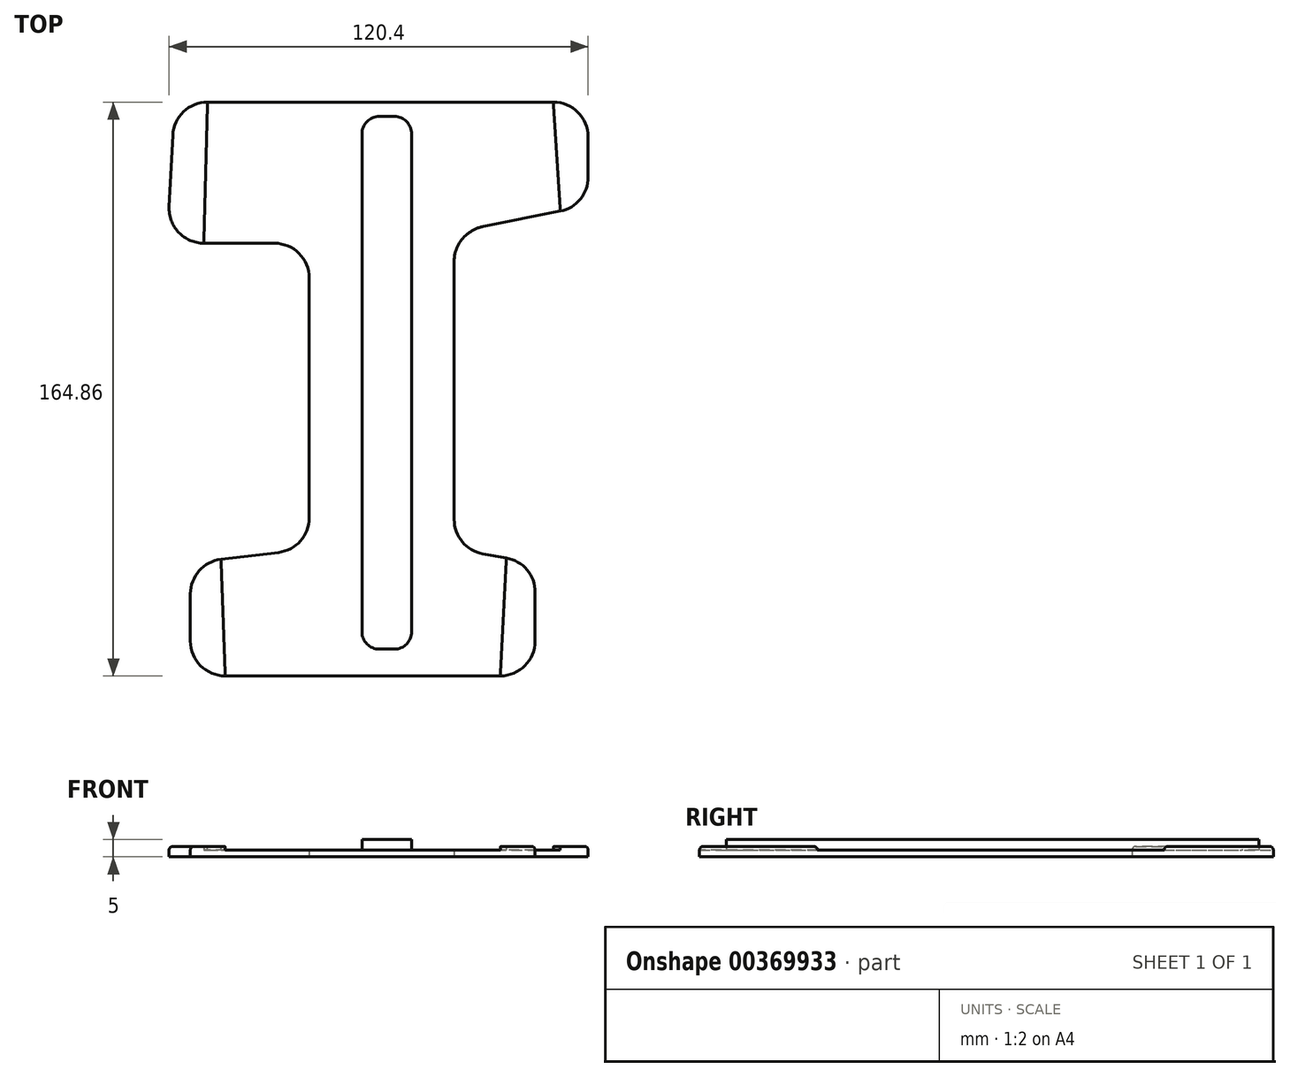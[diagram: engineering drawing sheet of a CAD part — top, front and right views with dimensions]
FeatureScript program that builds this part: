
annotation { "Feature Type Name" : "Feature", "Feature Type Description" : "" }
export const myFeature = defineFeature(function(context is Context, id is Id, definition is map)
    precondition{}
    {
        {
            var Q0;
            Q0=qCreatedBy(makeId("Top.planeOp"),FACE);
            var sketch = newSketch(context, id + "F0", { "sketchPlane" : qUnion([Q0])});
            skLineSegment(sketch, "E0", {"start": v(-44.38, 100.11) * mm, "end": v(55, 100.11) * mm});
            skLineSegment(sketch, "E1", {"start": v(65, 90.11) * mm, "end": v(65, 78.6) * mm});
            skLineSegment(sketch, "E2", {"start": v(56.95, 68.78) * mm, "end": v(34.8, 64.37) * mm});
            skLineSegment(sketch, "E3", {"start": v(30.52, 62.4) * mm, "end": v(30.27, 62.2) * mm});
            skLineSegment(sketch, "E4", {"start": v(26.49, 54.36) * mm, "end": v(26.49, -19.82) * mm});
            skLineSegment(sketch, "E5", {"start": v(34.74, -29.66) * mm, "end": v(41.5, -30.86) * mm});
            skLineSegment(sketch, "E6", {"start": v(49.76, -40.71) * mm, "end": v(49.76, -54.75) * mm});
            skLineSegment(sketch, "E7", {"start": v(39.76, -64.75) * mm, "end": v(-39.3, -64.75) * mm});
            skLineSegment(sketch, "E8", {"start": v(-49.3, -54.75) * mm, "end": v(-49.3, -41.2) * mm});
            skLineSegment(sketch, "E9", {"start": v(-40.5, -31.27) * mm, "end": v(-23.95, -29.26) * mm});
            skLineSegment(sketch, "E10", {"start": v(-15.15, -19.34) * mm, "end": v(-15.15, 49.57) * mm});
            skLineSegment(sketch, "E11", {"start": v(-25.15, 59.57) * mm, "end": v(-45.4, 59.57) * mm});
            skLineSegment(sketch, "E12", {"start": v(-55.4, 70.07) * mm, "end": v(-54.37, 90.6) * mm});
            skPoint(sketch, "E13.visualSharp", {"position": v(-55.91, 59.57) * mm});
            skArc(sketch, "E13.filletArc", {"start": v(-55.4, 70.07) * mm, "mid": v(-52.65, 62.68) * mm, "end": v(-45.4, 59.57) * mm});
            skPoint(sketch, "E14.visualSharp", {"position": v(-15.15, 59.57) * mm});
            skArc(sketch, "E14.filletArc", {"start": v(-15.15, 49.57) * mm, "mid": v(-18.08, 56.64) * mm, "end": v(-25.15, 59.57) * mm});
            skPoint(sketch, "E15.visualSharp", {"position": v(-53.9, 100.11) * mm});
            skArc(sketch, "E15.filletArc", {"start": v(-44.38, 100.11) * mm, "mid": v(-51.28, 97.35) * mm, "end": v(-54.37, 90.6) * mm});
            skPoint(sketch, "E16.visualSharp", {"position": v(65, 100.11) * mm});
            skArc(sketch, "E16.filletArc", {"start": v(65, 90.11) * mm, "mid": v(62.07, 97.18) * mm, "end": v(55, 100.11) * mm});
            skPoint(sketch, "E17.visualSharp", {"position": v(65, 70.39) * mm});
            skArc(sketch, "E17.filletArc", {"start": v(56.95, 68.78) * mm, "mid": v(62.73, 72.25) * mm, "end": v(65, 78.6) * mm});
            skPoint(sketch, "E18.visualSharp", {"position": v(32.42, 63.9) * mm});
            skArc(sketch, "E18.filletArc", {"start": v(34.8, 64.37) * mm, "mid": v(32.54, 63.64) * mm, "end": v(30.52, 62.4) * mm});
            skPoint(sketch, "E19.visualSharp", {"position": v(26.49, 59.2) * mm});
            skArc(sketch, "E19.filletArc", {"start": v(30.27, 62.2) * mm, "mid": v(27.48, 58.71) * mm, "end": v(26.49, 54.36) * mm});
            skPoint(sketch, "E20.visualSharp", {"position": v(-15.15, -28.2) * mm});
            skArc(sketch, "E20.filletArc", {"start": v(-23.95, -29.26) * mm, "mid": v(-17.67, -25.97) * mm, "end": v(-15.15, -19.34) * mm});
            skPoint(sketch, "E21.visualSharp", {"position": v(26.49, -28.2) * mm});
            skArc(sketch, "E21.filletArc", {"start": v(26.49, -19.82) * mm, "mid": v(28.83, -26.24) * mm, "end": v(34.74, -29.66) * mm});
            skPoint(sketch, "E22.visualSharp", {"position": v(49.76, -32.33) * mm});
            skArc(sketch, "E22.filletArc", {"start": v(49.76, -40.71) * mm, "mid": v(47.42, -34.29) * mm, "end": v(41.5, -30.86) * mm});
            skPoint(sketch, "E23.visualSharp", {"position": v(-49.3, -32.33) * mm});
            skArc(sketch, "E23.filletArc", {"start": v(-40.5, -31.27) * mm, "mid": v(-46.78, -34.56) * mm, "end": v(-49.3, -41.2) * mm});
            skPoint(sketch, "E24.visualSharp", {"position": v(49.76, -64.75) * mm});
            skArc(sketch, "E24.filletArc", {"start": v(39.76, -64.75) * mm, "mid": v(46.83, -61.82) * mm, "end": v(49.76, -54.75) * mm});
            skPoint(sketch, "E25.visualSharp", {"position": v(-49.3, -64.75) * mm});
            skArc(sketch, "E25.filletArc", {"start": v(-49.3, -54.75) * mm, "mid": v(-46.37, -61.82) * mm, "end": v(-39.3, -64.75) * mm});
            skSolve(sketch);
        }
        {
            var Q0;
            Q0=makeQuery(id+"F0.imprint","IMPRINT",FACE,{"disambiguationData":[TD([[makeQuery(id+"F0.imprint","IMPRINT",EDGE,{"derivedFrom":sQuery(id+"F0.wireOp",EDGE,"E0")}),-1.0]])]});
            extrude(context, id + "F1", {"entities" : qUnion([Q0]), "depth" : 2 * mm});
        }
        {
            var Q0;
            Q0=makeQuery(id+"F1.opExtrude","CAP_FACE",FACE,{"disambiguationData":[OSD([sQuery(id+"F0.wireOp",EDGE,"E0"),sQuery(id+"F0.wireOp",EDGE,"E1"),sQuery(id+"F0.wireOp",EDGE,"E2"),sQuery(id+"F0.wireOp",EDGE,"E3"),sQuery(id+"F0.wireOp",EDGE,"E4"),sQuery(id+"F0.wireOp",EDGE,"E5"),sQuery(id+"F0.wireOp",EDGE,"E6"),sQuery(id+"F0.wireOp",EDGE,"E7"),sQuery(id+"F0.wireOp",EDGE,"E8"),sQuery(id+"F0.wireOp",EDGE,"E9"),sQuery(id+"F0.wireOp",EDGE,"E10"),sQuery(id+"F0.wireOp",EDGE,"E11"),sQuery(id+"F0.wireOp",EDGE,"E12"),sQuery(id+"F0.wireOp",EDGE,"E13.filletArc"),sQuery(id+"F0.wireOp",EDGE,"E14.filletArc"),sQuery(id+"F0.wireOp",EDGE,"E15.filletArc"),sQuery(id+"F0.wireOp",EDGE,"E16.filletArc"),sQuery(id+"F0.wireOp",EDGE,"E17.filletArc"),sQuery(id+"F0.wireOp",EDGE,"E18.filletArc"),sQuery(id+"F0.wireOp",EDGE,"E19.filletArc"),sQuery(id+"F0.wireOp",EDGE,"E20.filletArc"),sQuery(id+"F0.wireOp",EDGE,"E21.filletArc"),sQuery(id+"F0.wireOp",EDGE,"E22.filletArc"),sQuery(id+"F0.wireOp",EDGE,"E23.filletArc"),sQuery(id+"F0.wireOp",EDGE,"E24.filletArc"),sQuery(id+"F0.wireOp",EDGE,"E25.filletArc")])],"isStart":false});
            var sketch = newSketch(context, id + "F2", { "sketchPlane" : qUnion([Q0])});
            skLineSegment(sketch, "E26", {"start": v(0, 91) * mm, "end": v(0, -52.06) * mm});
            skLineSegment(sketch, "E27", {"start": v(5, -57.06) * mm, "end": v(9.29, -57.06) * mm});
            skLineSegment(sketch, "E28", {"start": v(14.29, -52.06) * mm, "end": v(14.29, 91) * mm});
            skLineSegment(sketch, "E29", {"start": v(9.29, 96) * mm, "end": v(5, 96) * mm});
            skPoint(sketch, "E30.visualSharp", {"position": v(14.29, 96) * mm});
            skArc(sketch, "E30.filletArc", {"start": v(14.29, 91) * mm, "mid": v(12.82, 94.53) * mm, "end": v(9.29, 96) * mm});
            skPoint(sketch, "E31.visualSharp", {"position": v(0, 96) * mm});
            skArc(sketch, "E31.filletArc", {"start": v(5, 96) * mm, "mid": v(1.46, 94.53) * mm, "end": v(0, 91) * mm});
            skPoint(sketch, "E32.visualSharp", {"position": v(14.29, -57.06) * mm});
            skArc(sketch, "E32.filletArc", {"start": v(9.29, -57.06) * mm, "mid": v(12.82, -55.6) * mm, "end": v(14.29, -52.06) * mm});
            skPoint(sketch, "E33.visualSharp", {"position": v(0, -57.06) * mm});
            skArc(sketch, "E33.filletArc", {"start": v(0, -52.06) * mm, "mid": v(1.46, -55.6) * mm, "end": v(5, -57.06) * mm});
            skSolve(sketch);
        }
        {
            var Q0;
            Q0=makeQuery(id+"F2.imprint","IMPRINT",FACE,{"disambiguationData":[TD([[makeQuery(id+"F2.imprint","IMPRINT",EDGE,{"derivedFrom":sQuery(id+"F2.wireOp",EDGE,"E26")}),1.0]])]});
            extrude(context, id + "F3", {"entities" : qUnion([Q0]), "operationType" : NewBodyOperationType.ADD, "depth" : 3 * mm});
        }
        {
            var Q0;
            Q0=makeQuery(id+"F1.opExtrude","CAP_FACE",FACE,{"disambiguationData":[OSD([sQuery(id+"F0.wireOp",EDGE,"E0"),sQuery(id+"F0.wireOp",EDGE,"E1"),sQuery(id+"F0.wireOp",EDGE,"E2"),sQuery(id+"F0.wireOp",EDGE,"E3"),sQuery(id+"F0.wireOp",EDGE,"E4"),sQuery(id+"F0.wireOp",EDGE,"E5"),sQuery(id+"F0.wireOp",EDGE,"E6"),sQuery(id+"F0.wireOp",EDGE,"E7"),sQuery(id+"F0.wireOp",EDGE,"E8"),sQuery(id+"F0.wireOp",EDGE,"E9"),sQuery(id+"F0.wireOp",EDGE,"E10"),sQuery(id+"F0.wireOp",EDGE,"E11"),sQuery(id+"F0.wireOp",EDGE,"E12"),sQuery(id+"F0.wireOp",EDGE,"E13.filletArc"),sQuery(id+"F0.wireOp",EDGE,"E14.filletArc"),sQuery(id+"F0.wireOp",EDGE,"E15.filletArc"),sQuery(id+"F0.wireOp",EDGE,"E16.filletArc"),sQuery(id+"F0.wireOp",EDGE,"E17.filletArc"),sQuery(id+"F0.wireOp",EDGE,"E18.filletArc"),sQuery(id+"F0.wireOp",EDGE,"E19.filletArc"),sQuery(id+"F0.wireOp",EDGE,"E20.filletArc"),sQuery(id+"F0.wireOp",EDGE,"E21.filletArc"),sQuery(id+"F0.wireOp",EDGE,"E22.filletArc"),sQuery(id+"F0.wireOp",EDGE,"E23.filletArc"),sQuery(id+"F0.wireOp",EDGE,"E24.filletArc"),sQuery(id+"F0.wireOp",EDGE,"E25.filletArc")])],"isStart":false});
            var sketch = newSketch(context, id + "F4", { "sketchPlane" : qUnion([Q0])});
            skLineSegment(sketch, "E34", {"start": v(-44.38, 100.11) * mm, "end": v(55, 100.11) * mm});
            skLineSegment(sketch, "E35", {"start": v(65, 90.11) * mm, "end": v(65, 78.6) * mm});
            skLineSegment(sketch, "E36", {"start": v(56.95, 68.78) * mm, "end": v(43.5, 66.1) * mm});
            skLineSegment(sketch, "E37", {"start": v(39.23, 64.13) * mm, "end": v(30.27, 57) * mm});
            skLineSegment(sketch, "E38", {"start": v(26.49, 49.17) * mm, "end": v(26.49, -19.82) * mm});
            skLineSegment(sketch, "E39", {"start": v(34.74, -29.66) * mm, "end": v(41.5, -30.86) * mm});
            skLineSegment(sketch, "E40", {"start": v(49.76, -40.71) * mm, "end": v(49.76, -54.75) * mm});
            skLineSegment(sketch, "E41", {"start": v(39.76, -64.75) * mm, "end": v(-39.3, -64.75) * mm});
            skLineSegment(sketch, "E42", {"start": v(-49.3, -54.75) * mm, "end": v(-49.3, -41.2) * mm});
            skLineSegment(sketch, "E43", {"start": v(-40.5, -31.27) * mm, "end": v(-23.95, -29.26) * mm});
            skLineSegment(sketch, "E44", {"start": v(-15.15, -19.34) * mm, "end": v(-15.15, 49.57) * mm});
            skLineSegment(sketch, "E45", {"start": v(-25.15, 59.57) * mm, "end": v(-45.4, 59.57) * mm});
            skLineSegment(sketch, "E46", {"start": v(-55.4, 70.07) * mm, "end": v(-54.37, 90.6) * mm});
            skPoint(sketch, "E47.visualSharp", {"position": v(-55.91, 59.57) * mm});
            skArc(sketch, "E47.filletArc", {"start": v(-55.4, 70.07) * mm, "mid": v(-52.65, 62.68) * mm, "end": v(-45.4, 59.57) * mm});
            skPoint(sketch, "E48.visualSharp", {"position": v(-15.15, 59.57) * mm});
            skArc(sketch, "E48.filletArc", {"start": v(-15.15, 49.57) * mm, "mid": v(-18.08, 56.64) * mm, "end": v(-25.15, 59.57) * mm});
            skPoint(sketch, "E49.visualSharp", {"position": v(-53.9, 100.11) * mm});
            skArc(sketch, "E49.filletArc", {"start": v(-44.38, 100.11) * mm, "mid": v(-51.28, 97.35) * mm, "end": v(-54.37, 90.6) * mm});
            skPoint(sketch, "E50.visualSharp", {"position": v(65, 100.11) * mm});
            skArc(sketch, "E50.filletArc", {"start": v(65, 90.11) * mm, "mid": v(62.07, 97.18) * mm, "end": v(55, 100.11) * mm});
            skPoint(sketch, "E51.visualSharp", {"position": v(65, 70.39) * mm});
            skArc(sketch, "E51.filletArc", {"start": v(56.95, 68.78) * mm, "mid": v(62.73, 72.25) * mm, "end": v(65, 78.6) * mm});
            skPoint(sketch, "E52.visualSharp", {"position": v(41.13, 65.63) * mm});
            skArc(sketch, "E52.filletArc", {"start": v(43.5, 66.1) * mm, "mid": v(41.25, 65.37) * mm, "end": v(39.23, 64.13) * mm});
            skPoint(sketch, "E53.visualSharp", {"position": v(26.49, 54) * mm});
            skArc(sketch, "E53.filletArc", {"start": v(30.27, 57) * mm, "mid": v(27.48, 53.52) * mm, "end": v(26.49, 49.17) * mm});
            skPoint(sketch, "E54.visualSharp", {"position": v(-15.15, -28.2) * mm});
            skArc(sketch, "E54.filletArc", {"start": v(-23.95, -29.26) * mm, "mid": v(-17.67, -25.97) * mm, "end": v(-15.15, -19.34) * mm});
            skPoint(sketch, "E55.visualSharp", {"position": v(26.49, -28.2) * mm});
            skArc(sketch, "E55.filletArc", {"start": v(26.49, -19.82) * mm, "mid": v(28.83, -26.24) * mm, "end": v(34.74, -29.66) * mm});
            skPoint(sketch, "E56.visualSharp", {"position": v(49.76, -32.33) * mm});
            skArc(sketch, "E56.filletArc", {"start": v(49.76, -40.71) * mm, "mid": v(47.42, -34.29) * mm, "end": v(41.5, -30.86) * mm});
            skPoint(sketch, "E57.visualSharp", {"position": v(-49.3, -32.33) * mm});
            skArc(sketch, "E57.filletArc", {"start": v(-40.5, -31.27) * mm, "mid": v(-46.78, -34.56) * mm, "end": v(-49.3, -41.2) * mm});
            skPoint(sketch, "E58.visualSharp", {"position": v(49.76, -64.75) * mm});
            skArc(sketch, "E58.filletArc", {"start": v(39.76, -64.75) * mm, "mid": v(46.83, -61.82) * mm, "end": v(49.76, -54.75) * mm});
            skPoint(sketch, "E59.visualSharp", {"position": v(-49.3, -64.75) * mm});
            skArc(sketch, "E59.filletArc", {"start": v(-49.3, -54.75) * mm, "mid": v(-46.37, -61.82) * mm, "end": v(-39.3, -64.75) * mm});
            skLineSegment(sketch, "E60", {"start": v(-45.4, 59.57) * mm, "end": v(-44.38, 100.11) * mm});
            skLineSegment(sketch, "E61", {"start": v(56.95, 68.78) * mm, "end": v(55, 100.11) * mm});
            skLineSegment(sketch, "E62", {"start": v(41.5, -30.86) * mm, "end": v(39.76, -64.75) * mm});
            skLineSegment(sketch, "E63", {"start": v(-39.3, -64.75) * mm, "end": v(-40.5, -31.27) * mm});
            skSolve(sketch);
        }
        {
            var Q0;
            Q0=makeQuery(id+"F4.imprint","IMPRINT",FACE,{"disambiguationData":[TD([[makeQuery(id+"F4.imprint","IMPRINT",EDGE,{"derivedFrom":sQuery(id+"F4.wireOp",EDGE,"E42")}),-1.0]])]});
            var Q1;
            Q1=makeQuery(id+"F4.imprint","IMPRINT",FACE,{"disambiguationData":[TD([[makeQuery(id+"F4.imprint","IMPRINT",EDGE,{"derivedFrom":sQuery(id+"F4.wireOp",EDGE,"E40")}),-1.0]])]});
            var Q2;
            Q2=makeQuery(id+"F4.imprint","IMPRINT",FACE,{"disambiguationData":[TD([[makeQuery(id+"F4.imprint","IMPRINT",EDGE,{"derivedFrom":sQuery(id+"F4.wireOp",EDGE,"E46")}),-1.0]])]});
            var Q3;
            Q3=makeQuery(id+"F4.imprint","IMPRINT",FACE,{"disambiguationData":[TD([[makeQuery(id+"F4.imprint","IMPRINT",EDGE,{"derivedFrom":sQuery(id+"F4.wireOp",EDGE,"E35")}),-1.0]])]});
            extrude(context, id + "F5", {"entities" : qUnion([Q0, Q1, Q2, Q3]), "operationType" : NewBodyOperationType.ADD, "depth" : 1 * mm});
        }
        {
            var Q0;
            Q0=makeQuery(id+"F5.opExtrude","CAP_EDGE",EDGE,{"disambiguationData":[OSD([sQuery(id+"F4.wireOp",EDGE,"E58.filletArc")])],"isStart":false});
            var Q1;
            Q1=makeQuery(id+"F5.opExtrude","CAP_EDGE",EDGE,{"disambiguationData":[OSD([sQuery(id+"F4.wireOp",EDGE,"E40")])],"isStart":false});
            var Q2;
            Q2=makeQuery(id+"F5.opExtrude","CAP_EDGE",EDGE,{"disambiguationData":[OSD([sQuery(id+"F4.wireOp",EDGE,"E56.filletArc")])],"isStart":false});
            var Q3;
            Q3=makeQuery(id+"F5.opExtrude","CAP_EDGE",EDGE,{"disambiguationData":[OSD([sQuery(id+"F4.wireOp",EDGE,"E42")])],"isStart":false});
            var Q4;
            Q4=makeQuery(id+"F5.opExtrude","CAP_EDGE",EDGE,{"disambiguationData":[OSD([sQuery(id+"F4.wireOp",EDGE,"E57.filletArc")])],"isStart":false});
            var Q5;
            Q5=makeQuery(id+"F5.opExtrude","CAP_EDGE",EDGE,{"disambiguationData":[OSD([sQuery(id+"F4.wireOp",EDGE,"E46")])],"isStart":false});
            var Q6;
            Q6=makeQuery(id+"F5.opExtrude","CAP_EDGE",EDGE,{"disambiguationData":[OSD([sQuery(id+"F4.wireOp",EDGE,"E35")])],"isStart":false});
            fillet(context, id + "F6", {"entities" : qUnion([Q0, Q1, Q2, Q3, Q4, Q5, Q6]), "radius" : 1 * mm, "tangentPropagation" : true, "allowEdgeOverflow" : false});
        }
    });
